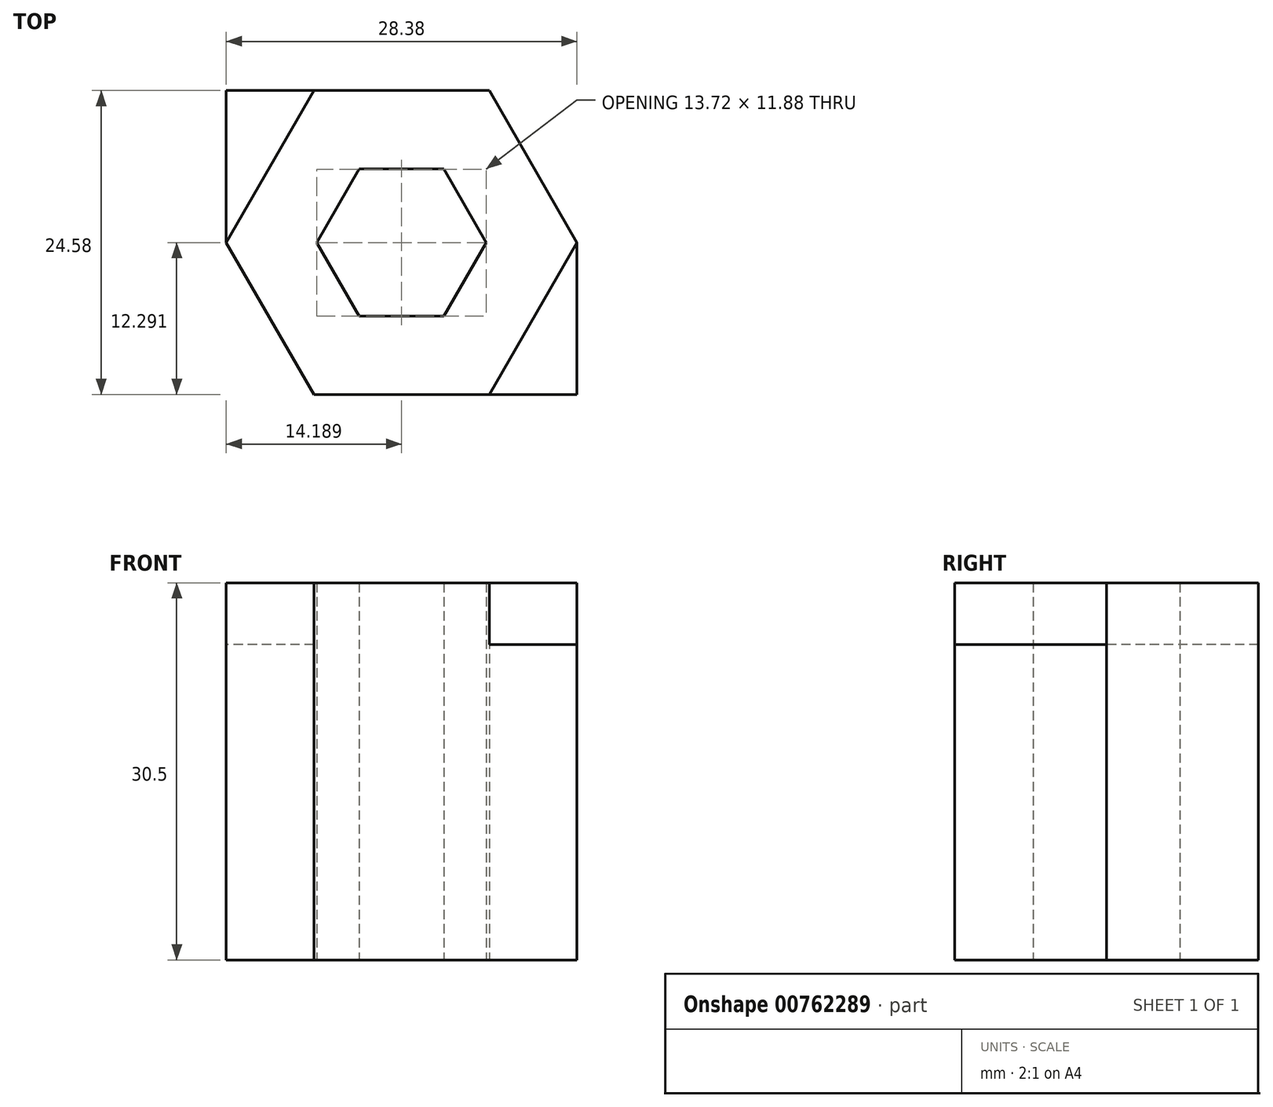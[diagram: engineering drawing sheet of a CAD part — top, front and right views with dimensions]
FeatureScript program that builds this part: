
annotation { "Feature Type Name" : "Feature", "Feature Type Description" : "" }
export const myFeature = defineFeature(function(context is Context, id is Id, definition is map)
    precondition{}
    {
        {
            var Q0;
            Q0=qCreatedBy(makeId("Top.planeOp"),FACE);
            var sketch = newSketch(context, id + "F0", { "sketchPlane" : qUnion([Q0])});
            skLineSegment(sketch, "E0", {"start": v(0, 0) * mm, "end": v(6.86, 0) * mm});
            skLineSegment(sketch, "E1", {"start": v(0, 0) * mm, "end": v(-3.43, -5.94) * mm});
            skLineSegment(sketch, "E2", {"start": v(-3.43, -5.94) * mm, "end": v(0, -11.88) * mm});
            skLineSegment(sketch, "E3", {"start": v(0, -11.88) * mm, "end": v(6.86, -11.88) * mm});
            skLineSegment(sketch, "E4", {"start": v(6.86, -11.88) * mm, "end": v(10.29, -5.94) * mm});
            skLineSegment(sketch, "E5", {"start": v(10.29, -5.94) * mm, "end": v(6.86, 0) * mm});
            skLineSegment(sketch, "E6.0", {"start": v(-3.67, 6.35) * mm, "end": v(10.52, 6.35) * mm});
            skLineSegment(sketch, "E6.1", {"start": v(-10.76, -5.94) * mm, "end": v(-3.67, -18.23) * mm});
            skLineSegment(sketch, "E6.2", {"start": v(-3.67, -18.23) * mm, "end": v(10.52, -18.23) * mm});
            skLineSegment(sketch, "E6.3", {"start": v(-3.67, 6.35) * mm, "end": v(-10.76, -5.94) * mm});
            skLineSegment(sketch, "E6.4", {"start": v(10.52, -18.23) * mm, "end": v(17.62, -5.94) * mm});
            skLineSegment(sketch, "E6.5", {"start": v(17.62, -5.94) * mm, "end": v(10.52, 6.35) * mm});
            skLineSegment(sketch, "E7", {"start": v(-10.76, -5.94) * mm, "end": v(-10.76, 6.35) * mm});
            skLineSegment(sketch, "E8", {"start": v(-10.76, 6.35) * mm, "end": v(-3.67, 6.35) * mm});
            skLineSegment(sketch, "E9", {"start": v(10.52, -18.23) * mm, "end": v(17.62, -18.23) * mm});
            skLineSegment(sketch, "E10", {"start": v(17.62, -18.23) * mm, "end": v(17.62, -5.94) * mm});
            skSolve(sketch);
        }
        {
            var Q0;
            Q0=makeQuery(id+"F0.imprint","IMPRINT",FACE,{"disambiguationData":[TD([[makeQuery(id+"F0.imprint","IMPRINT",EDGE,{"derivedFrom":sQuery(id+"F0.wireOp",EDGE,"E0")}),1.0]])]});
            extrude(context, id + "F1", {"entities" : qUnion([Q0]), "depth" : 30.5 * mm, "offsetDistance" : 25.4 * mm});
        }
        {
            var Q0;
            Q0=makeQuery(id+"F0.imprint","IMPRINT",FACE,{"disambiguationData":[TD([[makeQuery(id+"F0.imprint","IMPRINT",EDGE,{"derivedFrom":sQuery(id+"F0.wireOp",EDGE,"E6.4")}),-1.0]])]});
            var Q1;
            Q1=makeQuery(id+"F0.imprint","IMPRINT",FACE,{"disambiguationData":[TD([[makeQuery(id+"F0.imprint","IMPRINT",EDGE,{"derivedFrom":sQuery(id+"F0.wireOp",EDGE,"E6.3")}),-1.0]])]});
            extrude(context, id + "F2", {"entities" : qUnion([Q0, Q1]), "operationType" : NewBodyOperationType.ADD, "depth" : 25.5 * mm, "offsetDistance" : 25.4 * mm});
        }
    });
